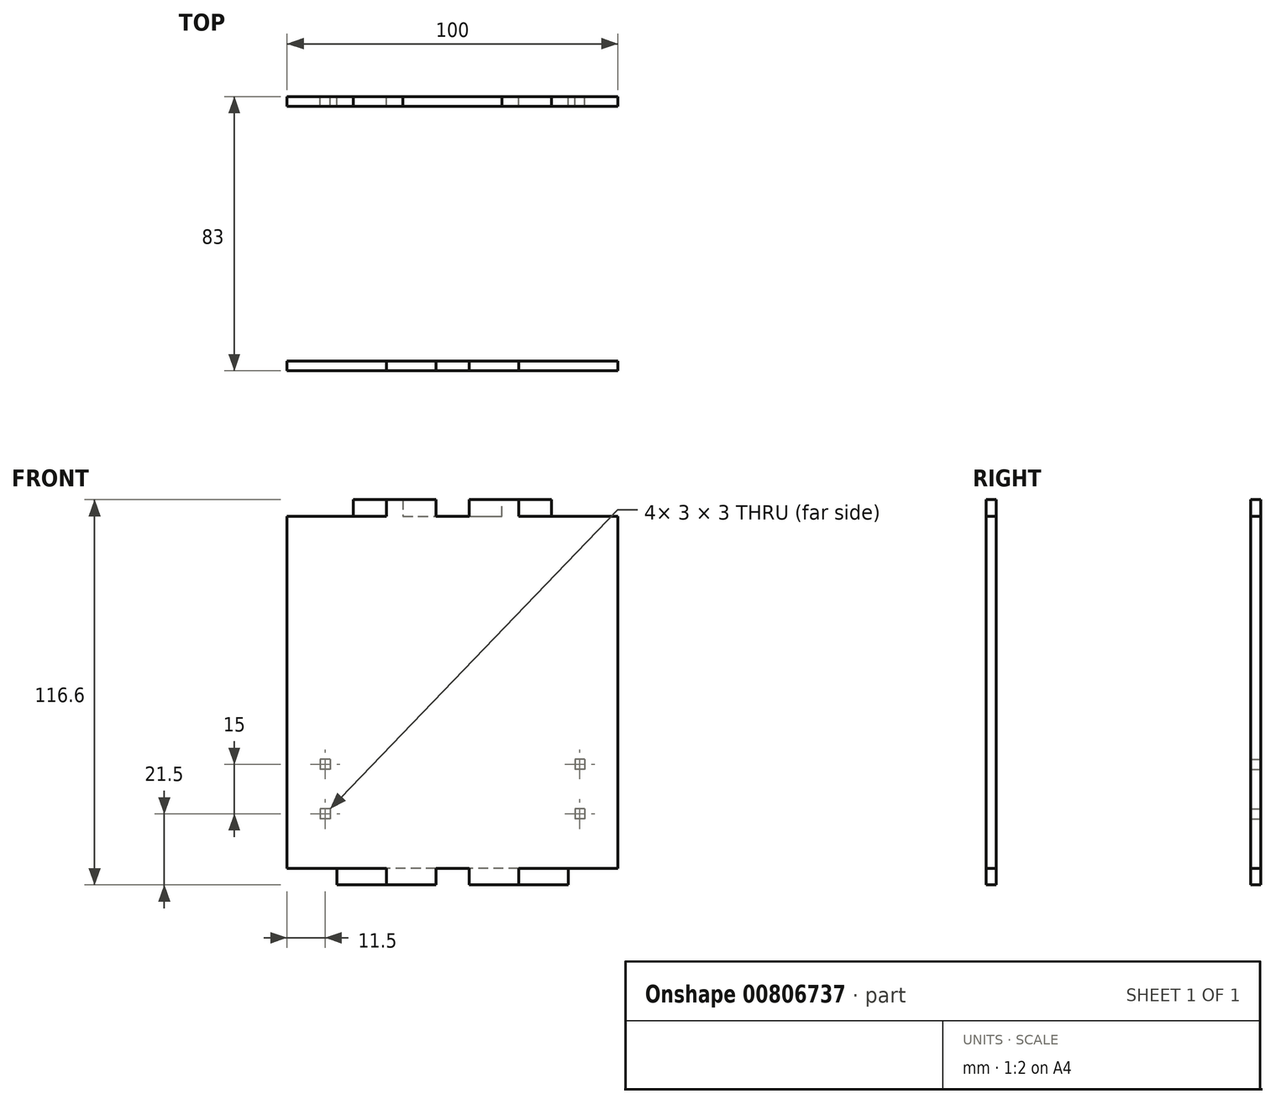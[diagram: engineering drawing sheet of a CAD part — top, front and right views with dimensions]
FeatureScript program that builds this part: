
annotation { "Feature Type Name" : "Feature", "Feature Type Description" : "" }
export const myFeature = defineFeature(function(context is Context, id is Id, definition is map)
    precondition{}
    {
        {
            var Q0;
            Q0=qCreatedBy(makeId("Front.planeOp"),FACE);
            var sketch = newSketch(context, id + "F0", { "sketchPlane" : qUnion([Q0])});
            skLineSegment(sketch, "E0", {"start": v(-50, 53.3) * mm, "end": v(-30, 53.3) * mm});
            skLineSegment(sketch, "E1", {"start": v(-30, 53.3) * mm, "end": v(-30, 58.3) * mm});
            skLineSegment(sketch, "E2", {"start": v(-30, 58.3) * mm, "end": v(-15, 58.3) * mm});
            skLineSegment(sketch, "E3", {"start": v(-15, 58.3) * mm, "end": v(-15, 53.3) * mm});
            skLineSegment(sketch, "E4", {"start": v(-15, 53.3) * mm, "end": v(15, 53.3) * mm});
            skLineSegment(sketch, "E5", {"start": v(15, 53.3) * mm, "end": v(15, 58.3) * mm});
            skLineSegment(sketch, "E6", {"start": v(15, 58.3) * mm, "end": v(30, 58.3) * mm});
            skLineSegment(sketch, "E7", {"start": v(30, 58.3) * mm, "end": v(30, 53.3) * mm});
            skLineSegment(sketch, "E8", {"start": v(30, 53.3) * mm, "end": v(50, 53.3) * mm});
            skLineSegment(sketch, "E9", {"start": v(50, 53.3) * mm, "end": v(50, -53.3) * mm});
            skLineSegment(sketch, "E10", {"start": v(50, -53.3) * mm, "end": v(35, -53.3) * mm});
            skLineSegment(sketch, "E11", {"start": v(35, -53.3) * mm, "end": v(35, -58.3) * mm});
            skLineSegment(sketch, "E12", {"start": v(35, -58.3) * mm, "end": v(20, -58.3) * mm});
            skLineSegment(sketch, "E13", {"start": v(20, -58.3) * mm, "end": v(20, -53.3) * mm});
            skLineSegment(sketch, "E14", {"start": v(20, -53.3) * mm, "end": v(-20, -53.3) * mm});
            skLineSegment(sketch, "E15", {"start": v(-20, -53.3) * mm, "end": v(-20, -58.3) * mm});
            skLineSegment(sketch, "E16", {"start": v(-20, -58.3) * mm, "end": v(-35, -58.3) * mm});
            skLineSegment(sketch, "E17", {"start": v(-35, -58.3) * mm, "end": v(-35, -53.3) * mm});
            skLineSegment(sketch, "E18", {"start": v(-35, -53.3) * mm, "end": v(-50, -53.3) * mm});
            skLineSegment(sketch, "E19", {"start": v(-50, -53.3) * mm, "end": v(-50, 53.3) * mm});
            skPoint(sketch, "E20", {"position": v(-50, 0) * mm});
            skLineSegment(sketch, "E21", {"start": v(-50, 0) * mm, "end": v(50, 0) * mm, "construction": true});
            skPoint(sketch, "E22", {"position": v(0, 0) * mm});
            skLineSegment(sketch, "E23.bottom", {"start": v(40, -20.3) * mm, "end": v(37, -20.3) * mm});
            skLineSegment(sketch, "E23.top", {"start": v(40, -23.3) * mm, "end": v(37, -23.3) * mm});
            skLineSegment(sketch, "E23.left", {"start": v(40, -20.3) * mm, "end": v(40, -23.3) * mm});
            skLineSegment(sketch, "E23.right", {"start": v(37, -20.3) * mm, "end": v(37, -23.3) * mm});
            skLineSegment(sketch, "E24.0.1.0", {"start": v(37, -35.3) * mm, "end": v(37, -38.3) * mm});
            skLineSegment(sketch, "E24.0.1.1", {"start": v(40, -35.3) * mm, "end": v(40, -38.3) * mm});
            skLineSegment(sketch, "E24.0.1.2", {"start": v(40, -38.3) * mm, "end": v(37, -38.3) * mm});
            skLineSegment(sketch, "E24.0.1.3", {"start": v(40, -35.3) * mm, "end": v(37, -35.3) * mm});
            skLineSegment(sketch, "E24.1.0.0", {"start": v(-40, -20.3) * mm, "end": v(-40, -23.3) * mm});
            skLineSegment(sketch, "E24.1.0.1", {"start": v(-37, -20.3) * mm, "end": v(-37, -23.3) * mm});
            skLineSegment(sketch, "E24.1.0.2", {"start": v(-37, -23.3) * mm, "end": v(-40, -23.3) * mm});
            skLineSegment(sketch, "E24.1.0.3", {"start": v(-37, -20.3) * mm, "end": v(-40, -20.3) * mm});
            skLineSegment(sketch, "E24.1.1.0", {"start": v(-40, -35.3) * mm, "end": v(-40, -38.3) * mm});
            skLineSegment(sketch, "E24.1.1.1", {"start": v(-37, -35.3) * mm, "end": v(-37, -38.3) * mm});
            skLineSegment(sketch, "E24.1.1.2", {"start": v(-37, -38.3) * mm, "end": v(-40, -38.3) * mm});
            skLineSegment(sketch, "E24.1.1.3", {"start": v(-37, -35.3) * mm, "end": v(-40, -35.3) * mm});
            skLineSegment(sketch, "E24.direction1", {"start": v(37, -23.3) * mm, "end": v(-40, -23.3) * mm, "construction": true});
            skLineSegment(sketch, "E24.direction2", {"start": v(37, -23.3) * mm, "end": v(37, -38.3) * mm, "construction": true});
            skSolve(sketch);
        }
        {
            var Q0;
            Q0=makeQuery(id+"F0.imprint","IMPRINT",FACE,{"disambiguationData":[TD([[makeQuery(id+"F0.imprint","IMPRINT",EDGE,{"derivedFrom":sQuery(id+"F0.wireOp",EDGE,"E0")}),-1.0]])]});
            extrude(context, id + "F1", {"entities" : qUnion([Q0]), "depth" : 3 * mm});
        }
        {
            var Q0;
            Q0=qCreatedBy(makeId("Front.planeOp"),FACE);
            cPlane(context, id + "F2", {"entities" : qUnion([Q0]), "cplaneType" : CPlaneType.OFFSET, "offset" : 80 * mm, "width" : 150 * mm, "height" : 150 * mm});
        }
        {
            var Q0;
            Q0=qCreatedBy(id+"F2.planeOp",FACE);
            var sketch = newSketch(context, id + "F3", { "sketchPlane" : qUnion([Q0])});
            skLineSegment(sketch, "E25", {"start": v(-50, 53.3) * mm, "end": v(-20, 53.3) * mm});
            skLineSegment(sketch, "E26", {"start": v(-20, 53.3) * mm, "end": v(-20, 58.3) * mm});
            skLineSegment(sketch, "E27", {"start": v(-20, 58.3) * mm, "end": v(-5, 58.3) * mm});
            skLineSegment(sketch, "E28", {"start": v(-5, 58.3) * mm, "end": v(-5, 53.3) * mm});
            skLineSegment(sketch, "E29", {"start": v(-5, 53.3) * mm, "end": v(5, 53.3) * mm});
            skLineSegment(sketch, "E30", {"start": v(5, 53.3) * mm, "end": v(5, 58.3) * mm});
            skLineSegment(sketch, "E31", {"start": v(5, 58.3) * mm, "end": v(20, 58.3) * mm});
            skLineSegment(sketch, "E32", {"start": v(20, 58.3) * mm, "end": v(20, 53.3) * mm});
            skLineSegment(sketch, "E33", {"start": v(20, 53.3) * mm, "end": v(50, 53.3) * mm});
            skLineSegment(sketch, "E34", {"start": v(50, 53.3) * mm, "end": v(50, -53.3) * mm});
            skLineSegment(sketch, "E35", {"start": v(50, -53.3) * mm, "end": v(20, -53.3) * mm});
            skLineSegment(sketch, "E36", {"start": v(20, -53.3) * mm, "end": v(20, -58.3) * mm});
            skLineSegment(sketch, "E37", {"start": v(20, -58.3) * mm, "end": v(5, -58.3) * mm});
            skLineSegment(sketch, "E38", {"start": v(5, -58.3) * mm, "end": v(5, -53.3) * mm});
            skLineSegment(sketch, "E39", {"start": v(5, -53.3) * mm, "end": v(-5, -53.3) * mm});
            skLineSegment(sketch, "E40", {"start": v(-5, -53.3) * mm, "end": v(-5, -58.3) * mm});
            skLineSegment(sketch, "E41", {"start": v(-5, -58.3) * mm, "end": v(-20, -58.3) * mm});
            skLineSegment(sketch, "E42", {"start": v(-20, -58.3) * mm, "end": v(-20, -53.3) * mm});
            skLineSegment(sketch, "E43", {"start": v(-20, -53.3) * mm, "end": v(-50, -53.3) * mm});
            skLineSegment(sketch, "E44", {"start": v(-50, -53.3) * mm, "end": v(-50, 53.3) * mm});
            skPoint(sketch, "E45", {"position": v(-50, 0) * mm});
            skLineSegment(sketch, "E46", {"start": v(-50, 0) * mm, "end": v(50, 0) * mm, "construction": true});
            skPoint(sketch, "E47", {"position": v(0, 0) * mm});
            skSolve(sketch);
        }
        {
            var Q0;
            Q0=makeQuery(id+"F3.imprint","IMPRINT",FACE,{"disambiguationData":[TD([[makeQuery(id+"F3.imprint","IMPRINT",EDGE,{"derivedFrom":sQuery(id+"F3.wireOp",EDGE,"E25")}),-1.0]])]});
            extrude(context, id + "F4", {"entities" : qUnion([Q0]), "depth" : 3 * mm});
        }
    });
